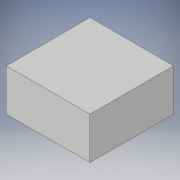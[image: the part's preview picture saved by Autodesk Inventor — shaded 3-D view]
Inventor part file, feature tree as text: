
AUTODESK INVENTOR PART (.ipt)
format: ipt  version: 2019 (Build 230136000, 136)  size: 86,016 bytes
history: native  units: mm
features: extrude x1, sketch x1
ambient origin geometry x8: Origin, YZ Plane, XZ Plane, XY Plane, X Axis, Y Axis, Z Axis, Center Point
bodies: Solid1 (feature_tree)
feature tree (2):
  extrude  "Extrusion1"  Depth=20.0mm
  sketch  "Sketch1"  dims[d0=20.0mm d1=20.0mm d2=10.0mm d3=0.0mm]
